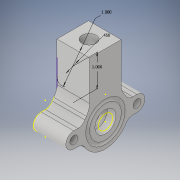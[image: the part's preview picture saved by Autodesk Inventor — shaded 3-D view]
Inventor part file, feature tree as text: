
AUTODESK INVENTOR PART (.ipt)
format: ipt  version: 2018 (Build 220112000, 112)  size: 283,136 bytes
history: native  units: in
note: dims shown in document units (in); Inventor stores cm internally (conversion verified against a paired STEP export)
features: sketch x8, other x5, extrude x4, projected_geometry x4, loft x3, revolve x2, fillet x2, pattern_circular x1
ambient origin geometry x8: Origin, YZ Plane, XZ Plane, XY Plane, X Axis, Y Axis, Z Axis, Center Point
bodies: Body1 (feature_tree)
feature tree (29):
  sketch  "Sketch2"  dims[d10=0.75in d11=0.65in]
  revolve  "Revolution1"  [1 undecoded]
  extrude  "Extrusion2"  Depth=0.25in
  fillet  "Fillet1"  Radius=1.0in
  pattern_circular  "Circular Pattern1"  Count=2 Angle=360.0deg
  revolve  "Revolution2"  [1 undecoded]
  extrude  "Extrusion8"  Depth=0.3325in
  sketch  "Sketch11"  dims[d23=1.0in d24=0.0in]
  extrude  "Extrusion9"  Depth=0.5in
  sketch  "Sketch14"  dims[d35=45.0deg d36=0.02in]
  loft  "Loft1"
  loft  "Loft2"
  loft  "Loft3"
  extrude  "Extrusion11"  Depth=0.5in
  fillet  "Fillet4"  Radius=1.0in
  sketch  "Sketch3"  dims[d13=90.0deg d20=0.25in d21=1.0in]
  sketch  "Sketch10"  dims[d22=0.5in]
  projected_geometry  "Projected Loop6"
  sketch  "Sketch12"  dims[d25=0.25in d26=0.7874in d27=360.0deg]
  projected_geometry  "Projected Loop7"
  sketch  "Sketch15"  dims[d38=0.225in d39=0.3325in]
  projected_geometry  "Projected Loop8"
  other  "Edges1"
  other  "Edges2"
  other  "Edges3"
  other  "Edges4"
  other  "Edges5"
  sketch  "Sketch16"  dims[d40=0.12in d41=0.5625in d42=90.0deg d60=0.275in d61=1.0in d62=0.45in d63=1.0in d64=0.5in d65=0.0in d67=0.125in d68=0.2in d69=0.2in d70=0.0in d71=0.75in d72=0.0in d75=0.45in d76=0.0in d77=90.0deg d78=0.0in d79=90.0deg d80=0.0in d81=90.0deg d82=0.0in d83=90.0deg d84=0.0in d85=90.0deg d86=0.0in d87=90.0deg d88=0.5in d89=0.0in d90=0.5in]
  projected_geometry  "Projected Loop9"
note: 2 required parameter values undecoded (feature->parameter linkage not recoverable at this tier; creation-order binding heuristic only, values carry confidence <= 0.55)
